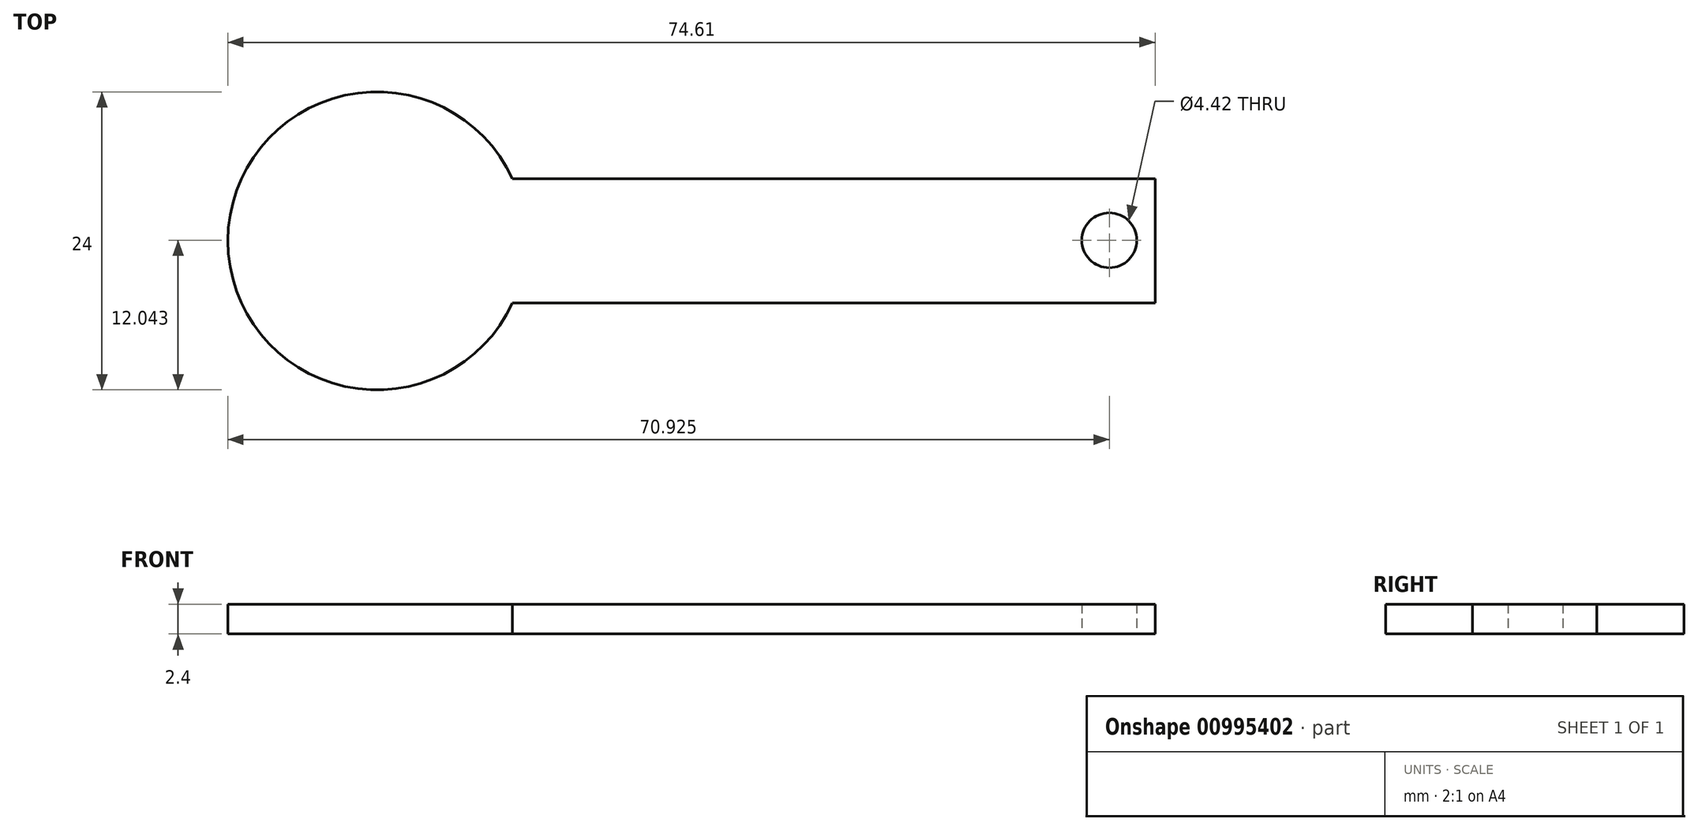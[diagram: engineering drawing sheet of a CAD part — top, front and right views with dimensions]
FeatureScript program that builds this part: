
annotation { "Feature Type Name" : "Feature", "Feature Type Description" : "" }
export const myFeature = defineFeature(function(context is Context, id is Id, definition is map)
    precondition{}
    {
        {
            var Q0;
            Q0=qCreatedBy(makeId("Top.planeOp"),FACE);
            var sketch = newSketch(context, id + "F0", { "sketchPlane" : qUnion([Q0])});
            skLineSegment(sketch, "E0.bottom", {"start": v(-1.7, 0) * mm, "end": v(50, 0) * mm});
            skLineSegment(sketch, "E0.top", {"start": v(-1.7, -10) * mm, "end": v(50, -10) * mm});
            skLineSegment(sketch, "E0.right", {"start": v(50, 0) * mm, "end": v(50, -10) * mm});
            skArc(sketch, "E1", {"start": v(-1.7, 0) * mm, "mid": v(-24.6, -5) * mm, "end": v(-1.7, -10) * mm});
            skPoint(sketch, "E1.centerSnap0", {"position": v(0, -5) * mm});
            skPoint(sketch, "E2.orphan", {"position": v(0, 0) * mm});
            skPoint(sketch, "E0.left.end.orphan", {"position": v(0, -10) * mm});
            skCircle(sketch, "E3", {"center": v(46.32, -4.96) * mm, "radius": 2.21 * mm});
            skSolve(sketch);
        }
        {
            var Q0;
            Q0=makeQuery(id+"F0.imprint","IMPRINT",FACE,{"disambiguationData":[TD([[makeQuery(id+"F0.imprint","IMPRINT",EDGE,{"derivedFrom":sQuery(id+"F0.wireOp",EDGE,"E0.bottom")}),-1.0]])]});
            var sketch = newSketch(context, id + "F1", { "sketchPlane" : qUnion([Q0])});
            skSolve(sketch);
        }
        {
            var Q0;
            Q0=makeQuery(id+"F1.imprint","IMPRINT",FACE,{"disambiguationData":[TD([[makeQuery(id+"F1.imprint","IMPRINT",EDGE,{"derivedFrom":makeQuery(id+"F0.imprint","IMPRINT",EDGE,{"derivedFrom":sQuery(id+"F0.wireOp",EDGE,"E0.bottom")})}),-1.0]])]});
            extrude(context, id + "F2", {"entities" : qUnion([Q0]), "depth" : 2.4 * mm, "offsetDistance" : 25 * mm});
        }
    });
